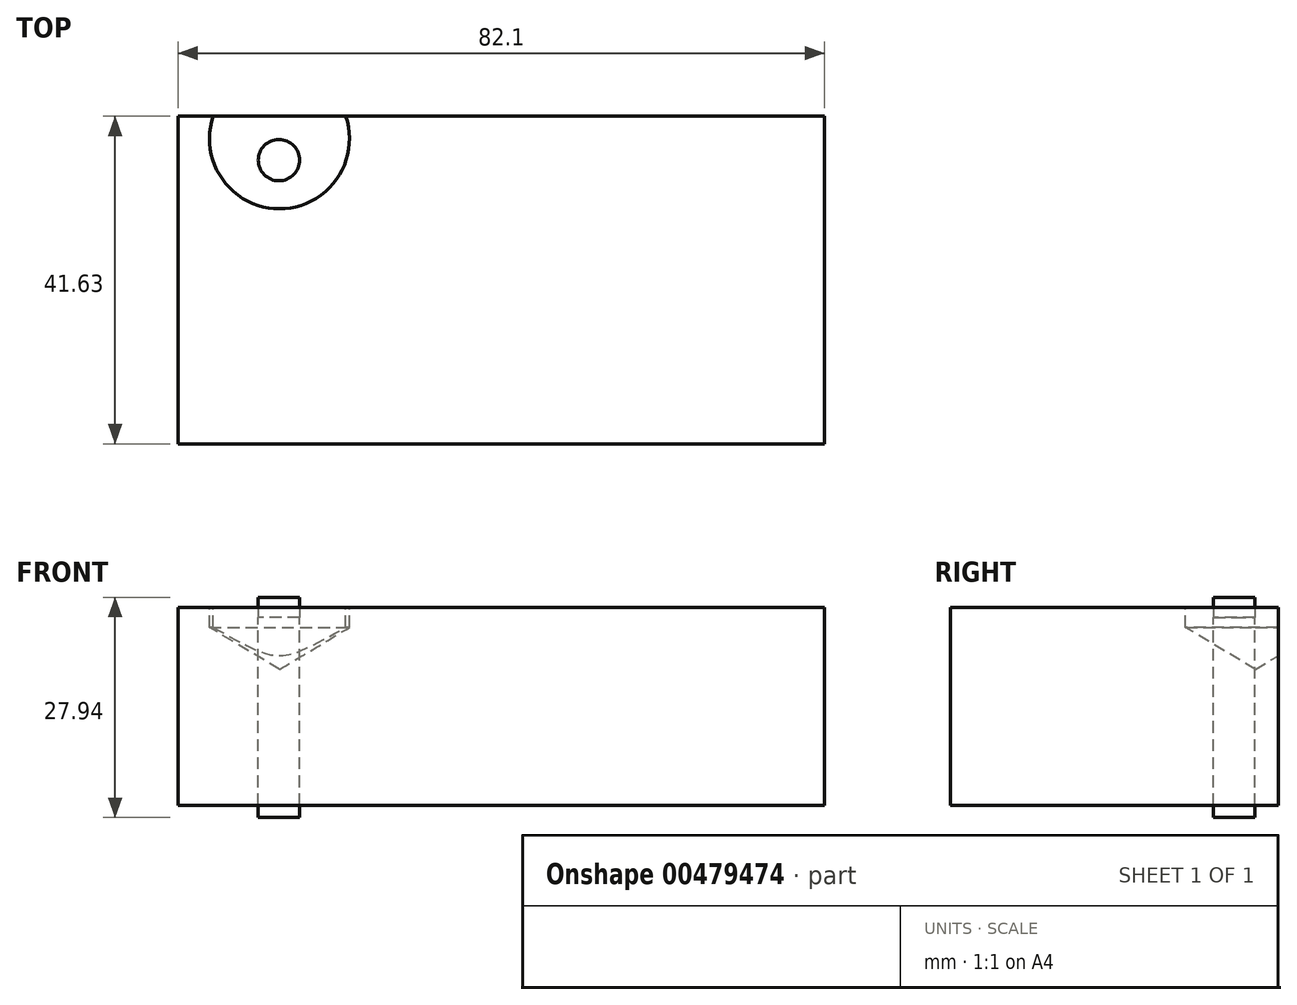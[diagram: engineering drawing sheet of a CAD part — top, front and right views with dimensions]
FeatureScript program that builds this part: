
annotation { "Feature Type Name" : "Feature", "Feature Type Description" : "" }
export const myFeature = defineFeature(function(context is Context, id is Id, definition is map)
    precondition{}
    {
        {
            var Q0;
            Q0=qCreatedBy(makeId("Top.planeOp"),FACE);
            var sketch = newSketch(context, id + "F0", { "sketchPlane" : qUnion([Q0])});
            skLineSegment(sketch, "E0.bottom", {"start": v(-40.47, 46.28) * mm, "end": v(41.63, 46.28) * mm});
            skLineSegment(sketch, "E0.top", {"start": v(-40.47, 4.65) * mm, "end": v(41.63, 4.65) * mm});
            skLineSegment(sketch, "E0.left", {"start": v(-40.47, 46.28) * mm, "end": v(-40.47, 4.65) * mm});
            skLineSegment(sketch, "E0.right", {"start": v(41.63, 46.28) * mm, "end": v(41.63, 4.65) * mm});
            skSolve(sketch);
        }
        {
            var Q0;
            Q0 = qSketchRegion(id + "F0", true);
            extrude(context, id + "F1", {"entities" : qUnion([Q0]), "depth" : 25.15 * mm});
        }
        {
            var Q0;
            Q0=makeQuery(id+"F1.opExtrude","CAP_FACE",FACE,{"disambiguationData":[OSD([sQuery(id+"F0.wireOp",EDGE,"E0.bottom"),sQuery(id+"F0.wireOp",EDGE,"E0.top"),sQuery(id+"F0.wireOp",EDGE,"E0.left"),sQuery(id+"F0.wireOp",EDGE,"E0.right")])],"isStart":false});
            var sketch = newSketch(context, id + "F2", { "sketchPlane" : qUnion([Q0])});
            skArc(sketch, "E1", {"start": v(-35.82, 46.28) * mm, "mid": v(-27.6, 34.69) * mm, "end": v(-19.36, 46.28) * mm});
            skCircle(sketch, "E2", {"center": v(-27.66, 40.7) * mm, "radius": 2.62 * mm});
            skSolve(sketch);
        }
        {
            var Q0;
            Q0=sQuery(id+"F2.wireOp",VERTEX,"E1.center");
            var Q1;
            Q1=makeQuery(id+"F1.opExtrude","SWEPT_BODY",BODY,{"disambiguationData":[OSD([sQuery(id+"F0.wireOp",EDGE,"E0.bottom"),sQuery(id+"F0.wireOp",EDGE,"E0.top"),sQuery(id+"F0.wireOp",EDGE,"E0.left"),sQuery(id+"F0.wireOp",EDGE,"E0.right")])]});
            hole(context, id + "F3", {"style" : HoleStyle.SIMPLE, "endStyle" : HoleEndStyle.BLIND, "holeDiameter" : 17.78 * mm, "holeDepth" : 2.54 * mm, "isTappedThrough" : true, "tappedDepth" : 12.7 * mm, "tapClearance" : 3, "startFromSketch" : true, "locations" : qUnion([Q0]), "scope" : qUnion([Q1])});
        }
        {
            var Q0;
            Q0=makeQuery(id+"F2.imprint","IMPRINT",FACE,{"disambiguationData":[TD([[makeQuery(id+"F2.imprint","IMPRINT",EDGE,{"derivedFrom":sQuery(id+"F2.wireOp",EDGE,"E2")}),1.0]])]});
            extrude(context, id + "F4", {"entities" : qUnion([Q0]), "endBound" : BoundingType.SYMMETRIC, "depth" : 2.54 * mm});
        }
        {
            var Q0;
            Q0=makeQuery(id+"F4.opExtrude","CAP_FACE",FACE,{"disambiguationData":[OSD([sQuery(id+"F2.wireOp",EDGE,"E2")])],"isStart":true});
            extrude(context, id + "F5", {"entities" : qUnion([Q0]), "depth" : 25.4 * mm});
        }
    });
